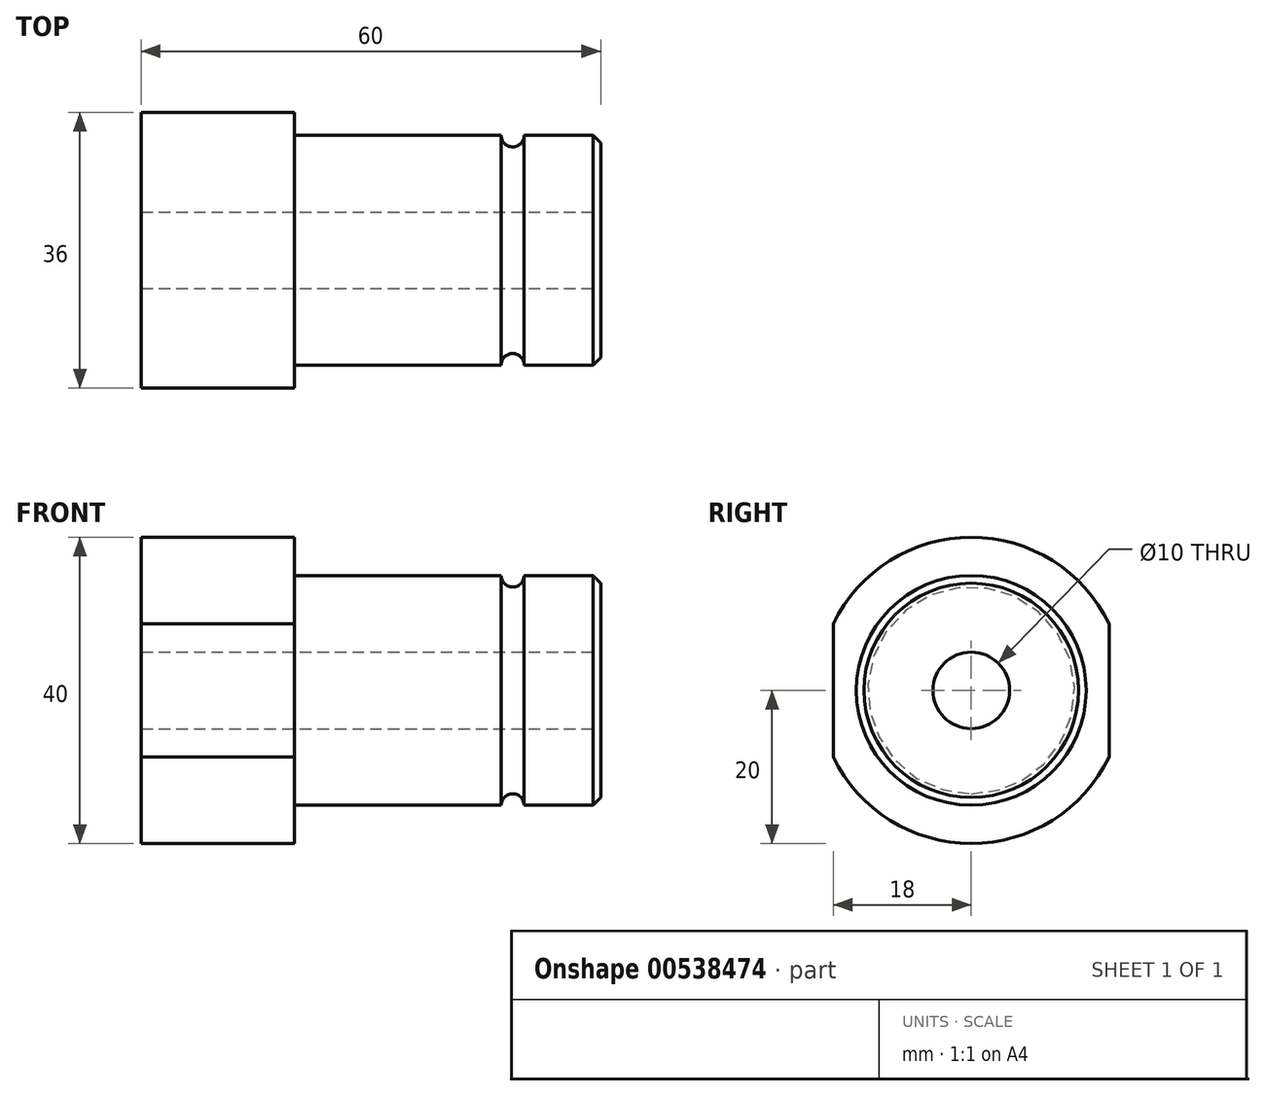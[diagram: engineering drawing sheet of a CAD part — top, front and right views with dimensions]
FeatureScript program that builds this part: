
annotation { "Feature Type Name" : "Feature", "Feature Type Description" : "" }
export const myFeature = defineFeature(function(context is Context, id is Id, definition is map)
    precondition{}
    {
        {
            var Q0;
            Q0=qCreatedBy(makeId("Front.planeOp"),FACE);
            var sketch = newSketch(context, id + "F0", { "sketchPlane" : qUnion([Q0])});
            skLineSegment(sketch, "E0", {"start": v(0, 0) * mm, "end": v(0, 20) * mm});
            skLineSegment(sketch, "E1", {"start": v(0, 20) * mm, "end": v(20, 20) * mm});
            skLineSegment(sketch, "E2", {"start": v(20, 20) * mm, "end": v(20, 15) * mm});
            skLineSegment(sketch, "E3", {"start": v(20, 15) * mm, "end": v(60, 15) * mm});
            skLineSegment(sketch, "E4", {"start": v(60, 15) * mm, "end": v(60, 0) * mm});
            skLineSegment(sketch, "E5", {"start": v(60, 0) * mm, "end": v(0, 0) * mm});
            skSolve(sketch);
        }
        {
            var Q0;
            Q0=qCreatedBy(makeId("Front.planeOp"),FACE);
            var sketch = newSketch(context, id + "F1", { "sketchPlane" : qUnion([Q0])});
            skLineSegment(sketch, "E6", {"start": v(-5.75, 0) * mm, "end": v(67.04, 0) * mm, "construction": true});
            skSolve(sketch);
        }
        {
            var Q0;
            Q0=makeQuery(id+"F0.imprint","IMPRINT",FACE,{"disambiguationData":[TD([[makeQuery(id+"F0.imprint","IMPRINT",EDGE,{"derivedFrom":sQuery(id+"F0.wireOp",EDGE,"E0")}),-1.0]])]});
            var Q1;
            Q1 = qSketchRegion(id + "F1", true);
            var Q2;
            Q2=sQuery(id+"F0.wireOp",EDGE,"E5");
            revolve(context, id + "F2", {"entities" : qUnion([Q0, Q1]), "axis" : qUnion([Q2]), "revolveType" : RevolveType.FULL});
        }
        {
            var Q0;
            Q0=qCreatedBy(makeId("Front.planeOp"),FACE);
            var sketch = newSketch(context, id + "F3", { "sketchPlane" : qUnion([Q0])});
            skCircle(sketch, "E7", {"center": v(48.5, 15) * mm, "radius": 1.5 * mm});
            skSolve(sketch);
        }
        {
            var Q0;
            Q0 = qSketchRegion(id + "F3", true);
            var Q1;
            Q1=makeQuery(id+"F2.opRevolve","SWEPT_FACE",FACE,{"disambiguationData":[OSD([sQuery(id+"F0.wireOp",EDGE,"E3")])]});
            revolve(context, id + "F4", {"operationType" : NewBodyOperationType.REMOVE, "entities" : qUnion([Q0]), "axis" : qUnion([Q1]), "revolveType" : RevolveType.FULL, "oppositeDirection" : true});
        }
        {
            var Q0;
            Q0=makeQuery(id+"F2.opRevolve","SWEPT_EDGE",EDGE,{"disambiguationData":[OSD([sQuery(id+"F0.wireOp",EDGE,"E3"),sQuery(id+"F0.wireOp",EDGE,"E4")])]});
            chamfer(context, id + "F5", {"entities" : qUnion([Q0]), "width" : 1 * mm, "tangentPropagation" : true});
        }
        {
            var Q0;
            Q0=makeQuery(id+"F2.opRevolve","SWEPT_FACE",FACE,{"disambiguationData":[OSD([sQuery(id+"F0.wireOp",EDGE,"E4")])]});
            var sketch = newSketch(context, id + "F6", { "sketchPlane" : qUnion([Q0])});
            skCircle(sketch, "E8", {"center": v(0, 0) * mm, "radius": 5 * mm});
            skSolve(sketch);
        }
        {
            var Q0;
            Q0 = qSketchRegion(id + "F6", true);
            extrude(context, id + "F7", {"entities" : qUnion([Q0]), "operationType" : NewBodyOperationType.REMOVE, "endBound" : BoundingType.THROUGH_ALL, "oppositeDirection" : true, "depth" : 25 * mm, "offsetDistance" : 25 * mm});
        }
        {
            var Q0;
            Q0=makeQuery(id+"F2.opRevolve","SWEPT_FACE",FACE,{"disambiguationData":[OSD([sQuery(id+"F0.wireOp",EDGE,"E0")])]});
            var sketch = newSketch(context, id + "F8", { "sketchPlane" : qUnion([Q0])});
            skLineSegment(sketch, "E9.bottom", {"start": v(18, -20) * mm, "end": v(-18, -20) * mm});
            skLineSegment(sketch, "E9.top", {"start": v(18, 20) * mm, "end": v(-18, 20) * mm});
            skLineSegment(sketch, "E9.left", {"start": v(18, -20) * mm, "end": v(18, 20) * mm});
            skLineSegment(sketch, "E9.right", {"start": v(-18, -20) * mm, "end": v(-18, 20) * mm});
            skPoint(sketch, "E9.middle", {"position": v(0, 0) * mm});
            skSolve(sketch);
        }
        {
            var Q0;
            {var subQ0=sQuery(id+"F8.wireOp",EDGE,"E9.right");var subQ1=makeQuery(id+"F2.opRevolve","SWEPT_EDGE",EDGE,{"disambiguationData":[OSD([sQuery(id+"F0.wireOp",EDGE,"E0"),sQuery(id+"F0.wireOp",EDGE,"E1")])]});var subQ2=makeQuery(id+"F8.imprint","INTERSECT",VERTEX,{"disambiguationData":[OD(0.0)],"derivedFrom":[subQ1,subQ0]});Q0=makeQuery(id+"F8.imprint","IMPRINT",FACE,{"disambiguationData":[TD([[makeQuery(id+"F8.imprint","IMPRINT",EDGE,{"disambiguationData":[TD([[subQ2,-1.0]])],"derivedFrom":subQ0}),1.0]])]});}
            var Q1;
            {var subQ0=sQuery(id+"F8.wireOp",EDGE,"E9.left");var subQ1=makeQuery(id+"F2.opRevolve","SWEPT_EDGE",EDGE,{"disambiguationData":[OSD([sQuery(id+"F0.wireOp",EDGE,"E0"),sQuery(id+"F0.wireOp",EDGE,"E1")])]});var subQ2=makeQuery(id+"F8.imprint","INTERSECT",VERTEX,{"disambiguationData":[OD(0.0)],"derivedFrom":[subQ1,subQ0]});Q1=makeQuery(id+"F8.imprint","IMPRINT",FACE,{"disambiguationData":[TD([[makeQuery(id+"F8.imprint","IMPRINT",EDGE,{"disambiguationData":[TD([[subQ2,-1.0]])],"derivedFrom":subQ0}),-1.0]])]});}
            extrude(context, id + "F9", {"entities" : qUnion([Q0, Q1]), "operationType" : NewBodyOperationType.REMOVE, "endBound" : BoundingType.UP_TO_NEXT, "oppositeDirection" : true, "depth" : 25 * mm, "offsetDistance" : 25 * mm});
        }
    });
